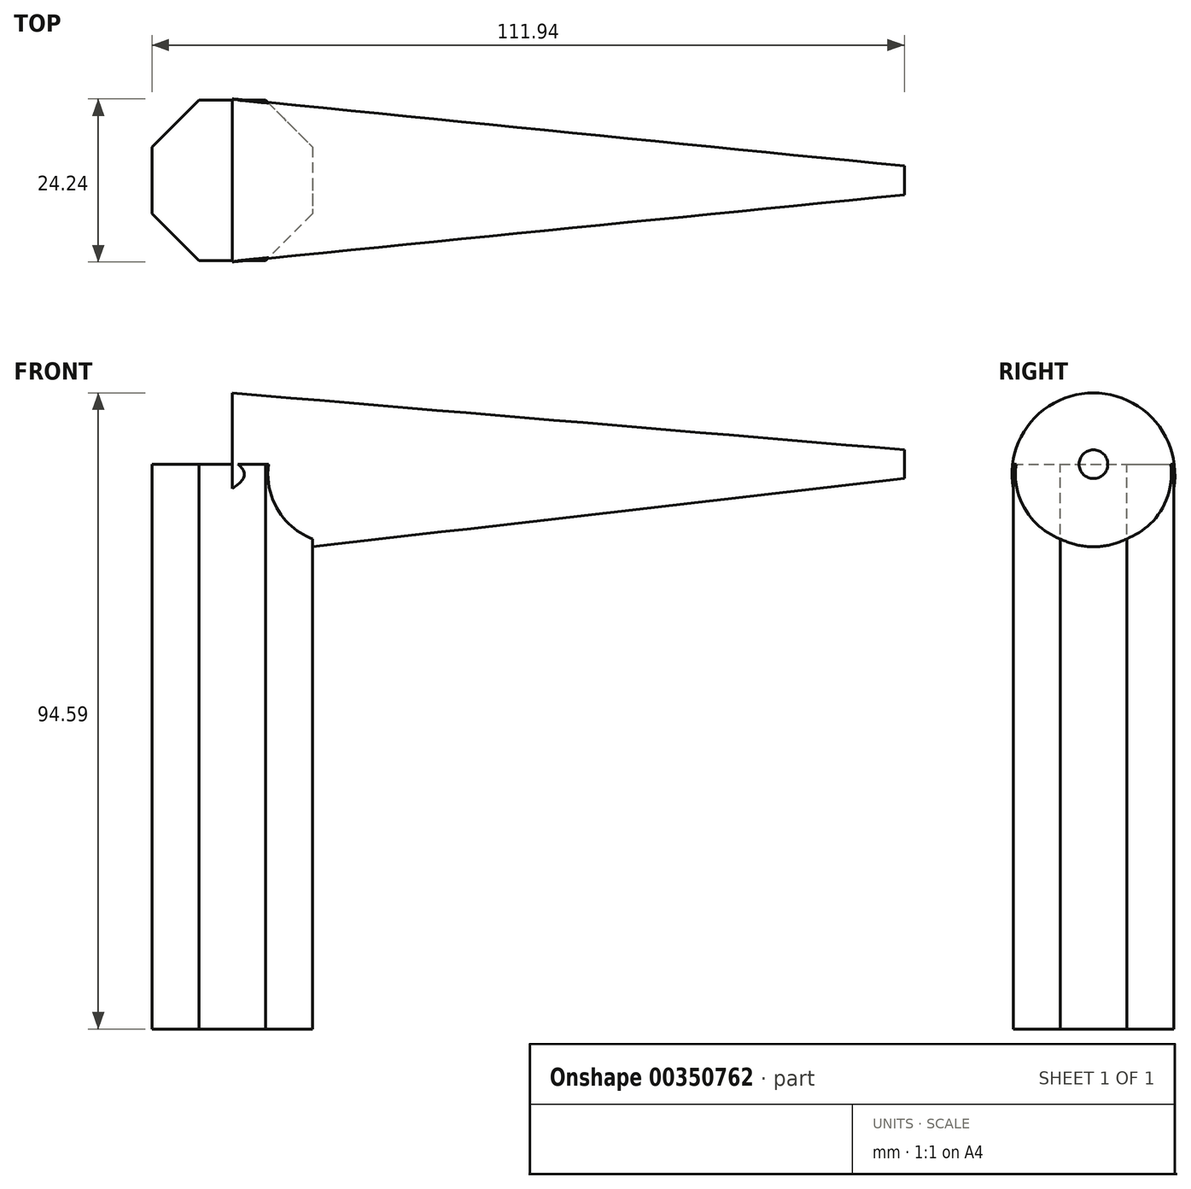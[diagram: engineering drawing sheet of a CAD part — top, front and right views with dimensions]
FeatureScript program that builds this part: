
annotation { "Feature Type Name" : "Feature", "Feature Type Description" : "" }
export const myFeature = defineFeature(function(context is Context, id is Id, definition is map)
    precondition{}
    {
        {
            var Q0;
            Q0=qCreatedBy(makeId("Top.planeOp"),FACE);
            var sketch = newSketch(context, id + "F0", { "sketchPlane" : qUnion([Q0])});
            skCircle(sketch, "E0.cCircle", {"center": v(0, 0) * mm, "radius": 11.94 * mm, "construction": true});
            skLineSegment(sketch, "E0.0", {"start": v(11.94, 4.95) * mm, "end": v(11.94, -4.95) * mm});
            skLineSegment(sketch, "E0.1", {"start": v(11.94, -4.95) * mm, "end": v(4.95, -11.94) * mm});
            skLineSegment(sketch, "E0.2", {"start": v(4.95, -11.94) * mm, "end": v(-4.95, -11.94) * mm});
            skLineSegment(sketch, "E0.3", {"start": v(-4.95, -11.94) * mm, "end": v(-11.94, -4.95) * mm});
            skLineSegment(sketch, "E0.4", {"start": v(-11.94, -4.95) * mm, "end": v(-11.94, 4.95) * mm});
            skLineSegment(sketch, "E0.5", {"start": v(-11.94, 4.95) * mm, "end": v(-4.95, 11.94) * mm});
            skLineSegment(sketch, "E0.6", {"start": v(-4.95, 11.94) * mm, "end": v(4.95, 11.94) * mm});
            skLineSegment(sketch, "E0.7", {"start": v(4.95, 11.94) * mm, "end": v(11.94, 4.95) * mm});
            skPoint(sketch, "E0.0.midPoint", {"position": v(11.94, 0) * mm});
            skSolve(sketch);
        }
        {
            var Q0;
            Q0=makeQuery(id+"F0.imprint","IMPRINT",FACE,{"disambiguationData":[TD([[makeQuery(id+"F0.imprint","IMPRINT",EDGE,{"derivedFrom":sQuery(id+"F0.wireOp",EDGE,"E0.0")}),-1.0]])]});
            extrude(context, id + "F1", {"entities" : qUnion([Q0]), "oppositeDirection" : true, "depth" : 84 * mm});
        }
        {
            var Q0;
            Q0=qCreatedBy(makeId("Right.planeOp"),FACE);
            var sketch = newSketch(context, id + "F2", { "sketchPlane" : qUnion([Q0])});
            skCircle(sketch, "E1", {"center": v(0, -1.53) * mm, "radius": 12.12 * mm});
            skSolve(sketch);
        }
        {
            var Q0;
            Q0=qCreatedBy(makeId("Right.planeOp"),FACE);
            cPlane(context, id + "F3", {"entities" : qUnion([Q0]), "cplaneType" : CPlaneType.OFFSET, "offset" : 100 * mm, "width" : 150 * mm, "height" : 150 * mm});
        }
        {
            var Q0;
            Q0=qCreatedBy(id+"F3.planeOp",FACE);
            var sketch = newSketch(context, id + "F4", { "sketchPlane" : qUnion([Q0])});
            skCircle(sketch, "E2", {"center": v(0, 0) * mm, "radius": 2.14 * mm});
            skSolve(sketch);
        }
        {
            var Q1;
            Q1=makeQuery(id+"F4.imprint","IMPRINT",FACE,{"disambiguationData":[TD([[makeQuery(id+"F4.imprint","IMPRINT",EDGE,{"derivedFrom":sQuery(id+"F4.wireOp",EDGE,"E2")}),1.0]])]});
            var Q2;
            Q2=makeQuery(id+"F2.imprint","IMPRINT",FACE,{"disambiguationData":[TD([[makeQuery(id+"F2.imprint","IMPRINT",EDGE,{"derivedFrom":sQuery(id+"F2.wireOp",EDGE,"E1")}),1.0]])]});
            loft(context, id + "F5", {"operationType" : NewBodyOperationType.ADD, "sheetProfilesArray" : [{ "sheetProfileEntities" : qUnion([Q1]) }, { "sheetProfileEntities" : qUnion([Q2]) }]});
        }
    });
